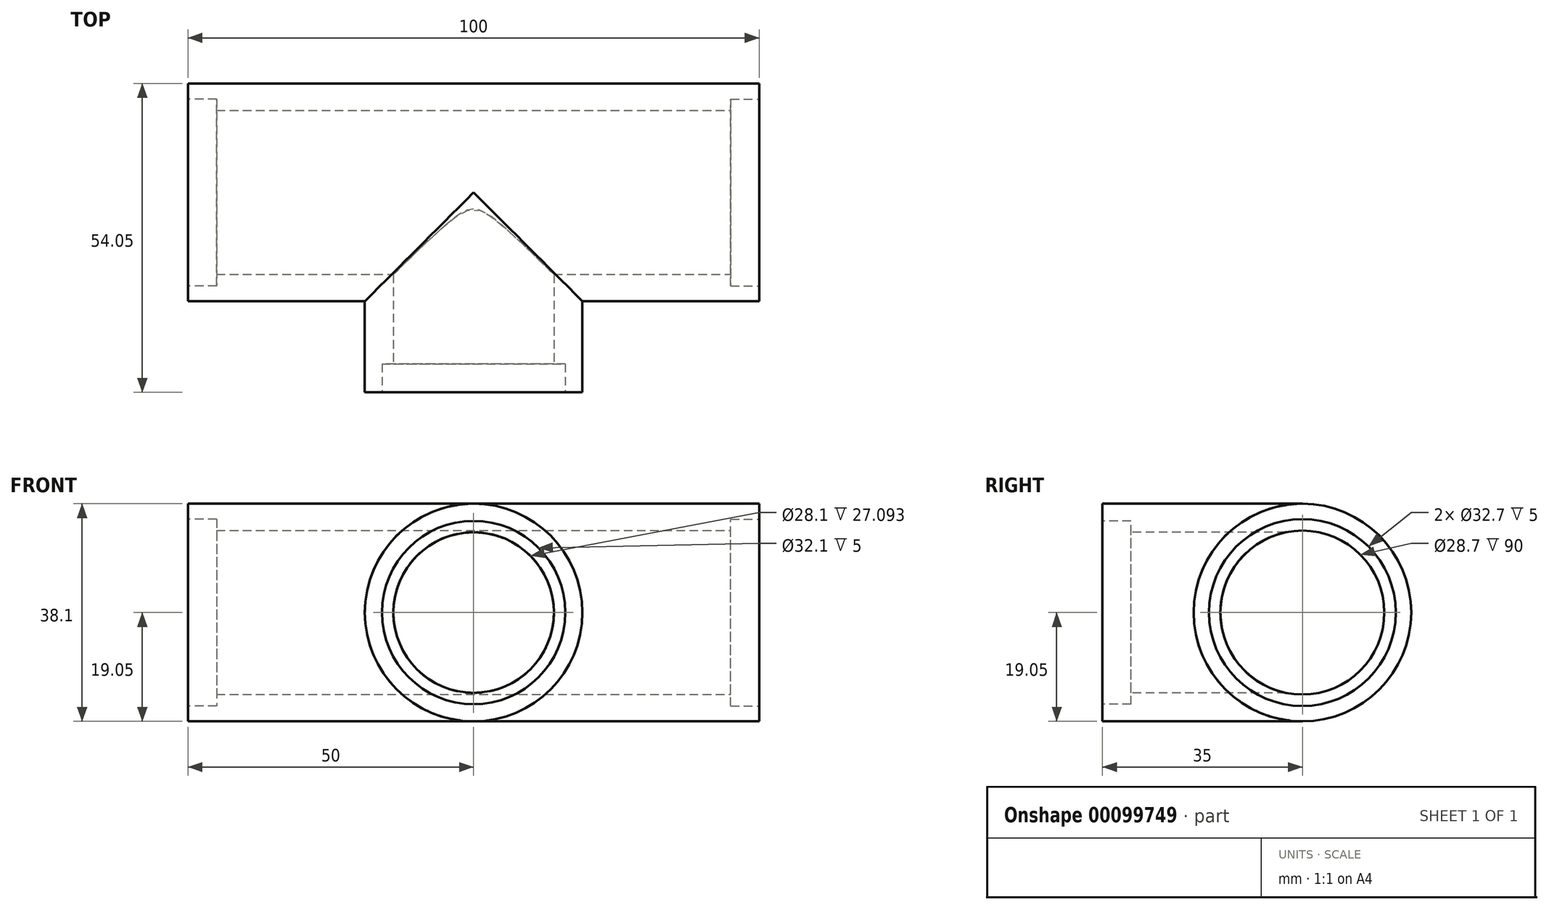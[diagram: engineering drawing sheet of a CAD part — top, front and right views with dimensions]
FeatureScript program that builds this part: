
annotation { "Feature Type Name" : "Feature", "Feature Type Description" : "" }
export const myFeature = defineFeature(function(context is Context, id is Id, definition is map)
    precondition{}
    {
        {
            var Q0;
            Q0=qCreatedBy(makeId("Right.planeOp"),FACE);
            var sketch = newSketch(context, id + "F0", { "sketchPlane" : qUnion([Q0])});
            skCircle(sketch, "E0", {"center": v(0, 0) * mm, "radius": 19.05 * mm});
            skSolve(sketch);
        }
        {
            var Q0;
            Q0=qCreatedBy(makeId("Front.planeOp"),FACE);
            var sketch = newSketch(context, id + "F1", { "sketchPlane" : qUnion([Q0])});
            skCircle(sketch, "E1", {"center": v(0, 0) * mm, "radius": 19.05 * mm});
            skLineSegment(sketch, "E2", {"start": v(-50, 19.05) * mm, "end": v(50, 19.05) * mm, "construction": true});
            skSolve(sketch);
        }
        {
            var Q0;
            Q0 = qSketchRegion(id + "F0", true);
            extrude(context, id + "F2", {"entities" : qUnion([Q0]), "endBound" : BoundingType.SYMMETRIC, "depth" : 100 * mm});
        }
        {
            var Q0;
            Q0=makeQuery(id+"F2.opExtrude","CAP_FACE",FACE,{"disambiguationData":[OSD([sQuery(id+"F0.wireOp",EDGE,"E0")])],"isStart":false});
            var sketch = newSketch(context, id + "F3", { "sketchPlane" : qUnion([Q0])});
            skCircle(sketch, "E3", {"center": v(0, 0) * mm, "radius": 14.35 * mm});
            skSolve(sketch);
        }
        {
            var Q0;
            Q0 = qSketchRegion(id + "F1", true);
            extrude(context, id + "F4", {"entities" : qUnion([Q0]), "operationType" : NewBodyOperationType.ADD, "depth" : 35 * mm});
        }
        {
            var Q0;
            Q0 = qSketchRegion(id + "F3", true);
            extrude(context, id + "F5", {"entities" : qUnion([Q0]), "operationType" : NewBodyOperationType.REMOVE, "endBound" : BoundingType.THROUGH_ALL, "oppositeDirection" : true, "depth" : 25 * mm});
        }
        {
            var Q0;
            Q0=makeQuery(id+"F4.opExtrude","CAP_FACE",FACE,{"disambiguationData":[OSD([sQuery(id+"F1.wireOp",EDGE,"E1")])],"isStart":false});
            var sketch = newSketch(context, id + "F6", { "sketchPlane" : qUnion([Q0])});
            skCircle(sketch, "E4", {"center": v(0, 0) * mm, "radius": 14.05 * mm});
            skSolve(sketch);
        }
        {
            var Q0;
            Q0 = qSketchRegion(id + "F6", true);
            extrude(context, id + "F7", {"entities" : qUnion([Q0]), "operationType" : NewBodyOperationType.REMOVE, "endBound" : BoundingType.UP_TO_NEXT, "oppositeDirection" : true, "depth" : 25 * mm});
        }
        {
            var Q0;
            Q0=makeQuery(id+"F4.opExtrude","CAP_FACE",FACE,{"disambiguationData":[OSD([sQuery(id+"F1.wireOp",EDGE,"E1")])],"isStart":false});
            var sketch = newSketch(context, id + "F8", { "sketchPlane" : qUnion([Q0])});
            skCircle(sketch, "E5", {"center": v(0, 0) * mm, "radius": 16.05 * mm});
            skSolve(sketch);
        }
        {
            var Q0;
            Q0 = qSketchRegion(id + "F8", true);
            extrude(context, id + "F9", {"entities" : qUnion([Q0]), "operationType" : NewBodyOperationType.REMOVE, "oppositeDirection" : true, "depth" : 5 * mm});
        }
        {
            var Q0;
            Q0=makeQuery(id+"F2.opExtrude","CAP_FACE",FACE,{"disambiguationData":[OSD([sQuery(id+"F0.wireOp",EDGE,"E0")])],"isStart":false});
            var sketch = newSketch(context, id + "F10", { "sketchPlane" : qUnion([Q0])});
            skCircle(sketch, "E6", {"center": v(0, 0) * mm, "radius": 16.35 * mm});
            skSolve(sketch);
        }
        {
            var Q0;
            Q0 = qSketchRegion(id + "F10", true);
            extrude(context, id + "F11", {"entities" : qUnion([Q0]), "operationType" : NewBodyOperationType.REMOVE, "oppositeDirection" : true, "depth" : 5 * mm});
        }
        {
            var Q0;
            Q0=makeQuery(id+"F2.opExtrude","CAP_FACE",FACE,{"disambiguationData":[OSD([sQuery(id+"F0.wireOp",EDGE,"E0")])],"isStart":true});
            var sketch = newSketch(context, id + "F12", { "sketchPlane" : qUnion([Q0])});
            skCircle(sketch, "E7", {"center": v(0, 0) * mm, "radius": 16.35 * mm});
            skSolve(sketch);
        }
        {
            var Q0;
            Q0 = qSketchRegion(id + "F12", true);
            extrude(context, id + "F13", {"entities" : qUnion([Q0]), "operationType" : NewBodyOperationType.REMOVE, "oppositeDirection" : true, "depth" : 5 * mm});
        }
    });
